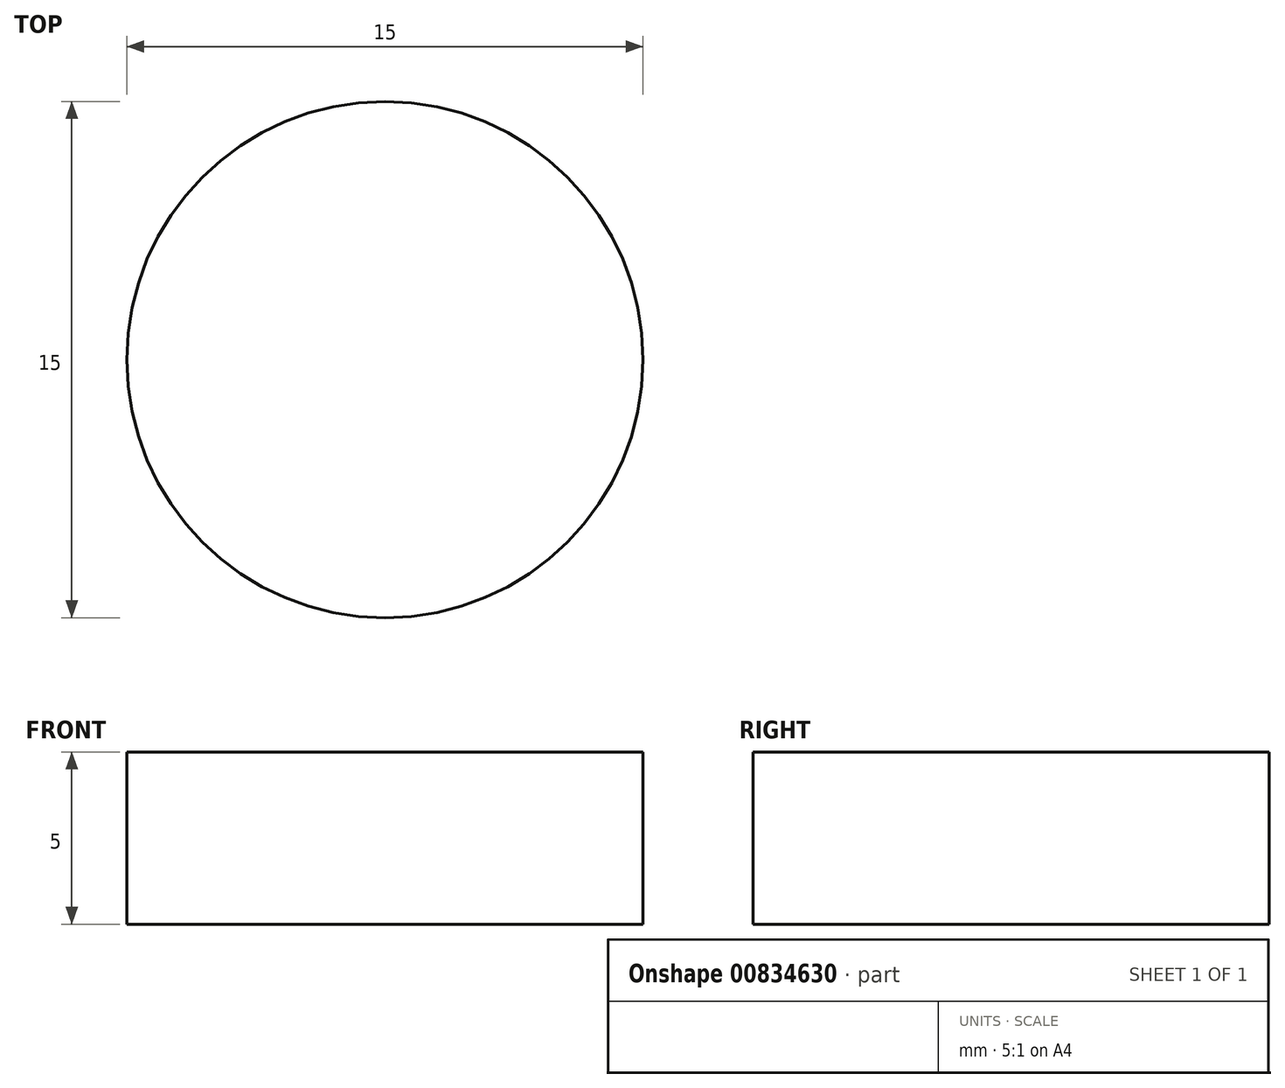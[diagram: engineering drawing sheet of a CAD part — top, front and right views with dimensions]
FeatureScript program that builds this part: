
annotation { "Feature Type Name" : "Feature", "Feature Type Description" : "" }
export const myFeature = defineFeature(function(context is Context, id is Id, definition is map)
    precondition{}
    {
        {
            var Q0;
            Q0=qCreatedBy(makeId("Top.planeOp"),FACE);
            var sketch = newSketch(context, id + "F0", { "sketchPlane" : qUnion([Q0])});
            skCircle(sketch, "E0", {"center": v(0, 0) * mm, "radius": 7.5 * mm});
            skSolve(sketch);
        }
        {
            var Q0;
            Q0 = qSketchRegion(id + "F0", true);
            extrude(context, id + "F1", {"entities" : qUnion([Q0]), "depth" : 5 * mm, "offsetDistance" : 25 * mm});
        }
    });
